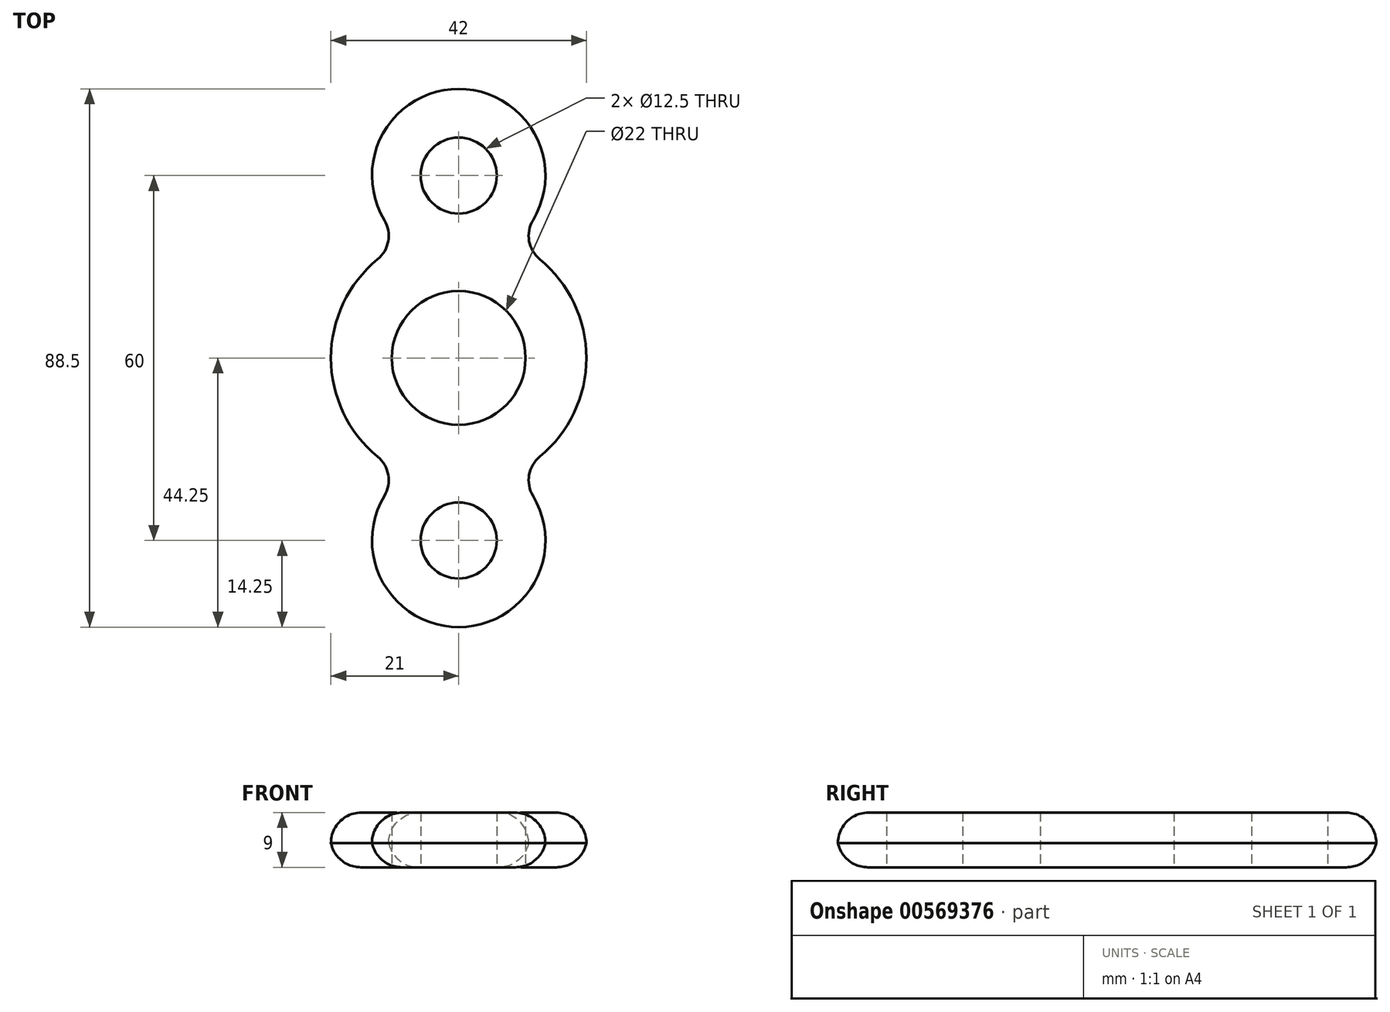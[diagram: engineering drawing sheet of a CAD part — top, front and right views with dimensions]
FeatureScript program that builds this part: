
annotation { "Feature Type Name" : "Feature", "Feature Type Description" : "" }
export const myFeature = defineFeature(function(context is Context, id is Id, definition is map)
    precondition{}
    {
        {
            var Q0;
            Q0=qCreatedBy(makeId("Top.planeOp"),FACE);
            var sketch = newSketch(context, id + "F0", { "sketchPlane" : qUnion([Q0])});
            skCircle(sketch, "E0", {"center": v(0, 0) * mm, "radius": 11 * mm});
            skCircle(sketch, "E1", {"center": v(0, -30) * mm, "radius": 6.25 * mm});
            skCircle(sketch, "E2", {"center": v(0, 30) * mm, "radius": 6.25 * mm});
            skCircle(sketch, "E3.0", {"center": v(0, 0) * mm, "radius": 21 * mm});
            skCircle(sketch, "E4.0", {"center": v(0, 30) * mm, "radius": 14.25 * mm});
            skCircle(sketch, "E5.0", {"center": v(0, -30) * mm, "radius": 14.25 * mm});
            skSolve(sketch);
        }
        {
            var Q0;
            Q0=makeQuery(id+"F0.imprint","IMPRINT",FACE,{"disambiguationData":[TD([[makeQuery(id+"F0.imprint","IMPRINT",EDGE,{"derivedFrom":sQuery(id+"F0.wireOp",EDGE,"E1")}),-1.0]])]});
            var Q1;
            Q1=makeQuery(id+"F0.imprint","IMPRINT",FACE,{"disambiguationData":[TD([[makeQuery(id+"F0.imprint","IMPRINT",EDGE,{"derivedFrom":sQuery(id+"F0.wireOp",EDGE,"E0")}),-1.0]])]});
            var Q2;
            {var subQ0=sQuery(id+"F0.wireOp",EDGE,"E5.0");var subQ1=sQuery(id+"F0.wireOp",EDGE,"E3.0");var subQ2=makeQuery(id+"F0.imprint","INTERSECT",VERTEX,{"disambiguationData":[OD(0.0)],"derivedFrom":[subQ1,subQ0]});Q2=makeQuery(id+"F0.imprint","IMPRINT",FACE,{"disambiguationData":[TD([[makeQuery(id+"F0.imprint","IMPRINT",EDGE,{"disambiguationData":[TD([[subQ2,-1.0]])],"derivedFrom":subQ1}),1.0]])]});}
            var Q3;
            {var subQ0=sQuery(id+"F0.wireOp",EDGE,"E4.0");var subQ1=sQuery(id+"F0.wireOp",EDGE,"E3.0");var subQ2=makeQuery(id+"F0.imprint","INTERSECT",VERTEX,{"disambiguationData":[OD(0.0)],"derivedFrom":[subQ1,subQ0]});Q3=makeQuery(id+"F0.imprint","IMPRINT",FACE,{"disambiguationData":[TD([[makeQuery(id+"F0.imprint","IMPRINT",EDGE,{"disambiguationData":[TD([[subQ2,1.0]])],"derivedFrom":subQ1}),1.0]])]});}
            var Q4;
            Q4=makeQuery(id+"F0.imprint","IMPRINT",FACE,{"disambiguationData":[TD([[makeQuery(id+"F0.imprint","IMPRINT",EDGE,{"derivedFrom":sQuery(id+"F0.wireOp",EDGE,"E2")}),-1.0]])]});
            extrude(context, id + "F1", {"entities" : qUnion([Q0, Q1, Q2, Q3, Q4]), "depth" : 9 * mm, "offsetDistance" : 25 * mm});
        }
        {
            var Q0;
            {var subQ0=sQuery(id+"F0.wireOp",EDGE,"E5.0");var subQ1=sQuery(id+"F0.wireOp",EDGE,"E3.0");Q0=makeQuery(id+"F1.opExtrude","SWEPT_EDGE",EDGE,{"disambiguationData":[OSD([subQ1,subQ0]),TDD([makeQuery(id+"F0.imprint","INTERSECT",VERTEX,{"disambiguationData":[OD(1.0)],"derivedFrom":[subQ1,subQ0]})])]});}
            fillet(context, id + "F2", {"entities" : qUnion([Q0]), "radius" : 5 * mm, "tangentPropagation" : true, "allowEdgeOverflow" : false});
        }
        {
            var Q0;
            {var subQ0=sQuery(id+"F0.wireOp",EDGE,"E4.0");var subQ1=sQuery(id+"F0.wireOp",EDGE,"E3.0");Q0=makeQuery(id+"F1.opExtrude","SWEPT_EDGE",EDGE,{"disambiguationData":[OSD([subQ1,subQ0]),TDD([makeQuery(id+"F0.imprint","INTERSECT",VERTEX,{"disambiguationData":[OD(1.0)],"derivedFrom":[subQ1,subQ0]})])]});}
            fillet(context, id + "F3", {"entities" : qUnion([Q0]), "radius" : 5 * mm, "tangentPropagation" : true, "allowEdgeOverflow" : false});
        }
        {
            var Q0;
            {var subQ0=sQuery(id+"F0.wireOp",EDGE,"E4.0");var subQ1=sQuery(id+"F0.wireOp",EDGE,"E3.0");Q0=makeQuery(id+"F1.opExtrude","SWEPT_EDGE",EDGE,{"disambiguationData":[OSD([subQ1,subQ0]),TDD([makeQuery(id+"F0.imprint","INTERSECT",VERTEX,{"disambiguationData":[OD(0.0)],"derivedFrom":[subQ1,subQ0]})])]});}
            var Q1;
            {var subQ0=sQuery(id+"F0.wireOp",EDGE,"E5.0");var subQ1=sQuery(id+"F0.wireOp",EDGE,"E3.0");Q1=makeQuery(id+"F1.opExtrude","SWEPT_EDGE",EDGE,{"disambiguationData":[OSD([subQ1,subQ0]),TDD([makeQuery(id+"F0.imprint","INTERSECT",VERTEX,{"disambiguationData":[OD(0.0)],"derivedFrom":[subQ1,subQ0]})])]});}
            fillet(context, id + "F4", {"entities" : qUnion([Q0, Q1]), "radius" : 5 * mm, "tangentPropagation" : true, "allowEdgeOverflow" : false});
        }
        {
            var Q0;
            Q0=makeQuery(id+"F1.opExtrude","CAP_EDGE",EDGE,{"disambiguationData":[OSD([sQuery(id+"F0.wireOp",EDGE,"E4.0")])],"isStart":false});
            fillet(context, id + "F5", {"entities" : qUnion([Q0]), "radius" : 5 * mm, "tangentPropagation" : true, "allowEdgeOverflow" : false});
        }
        {
            var Q0;
            Q0=makeQuery(id+"F1.opExtrude","CAP_EDGE",EDGE,{"disambiguationData":[OSD([sQuery(id+"F0.wireOp",EDGE,"E5.0")])],"isStart":true});
            var Q1;
            Q1=makeQuery(id+"F1.opExtrude","CAP_EDGE",EDGE,{"disambiguationData":[OSD([sQuery(id+"F0.wireOp",EDGE,"E4.0")])],"isStart":true});
            fillet(context, id + "F6", {"entities" : qUnion([Q0, Q1]), "radius" : 5 * mm, "tangentPropagation" : true, "allowEdgeOverflow" : false});
        }
    });
